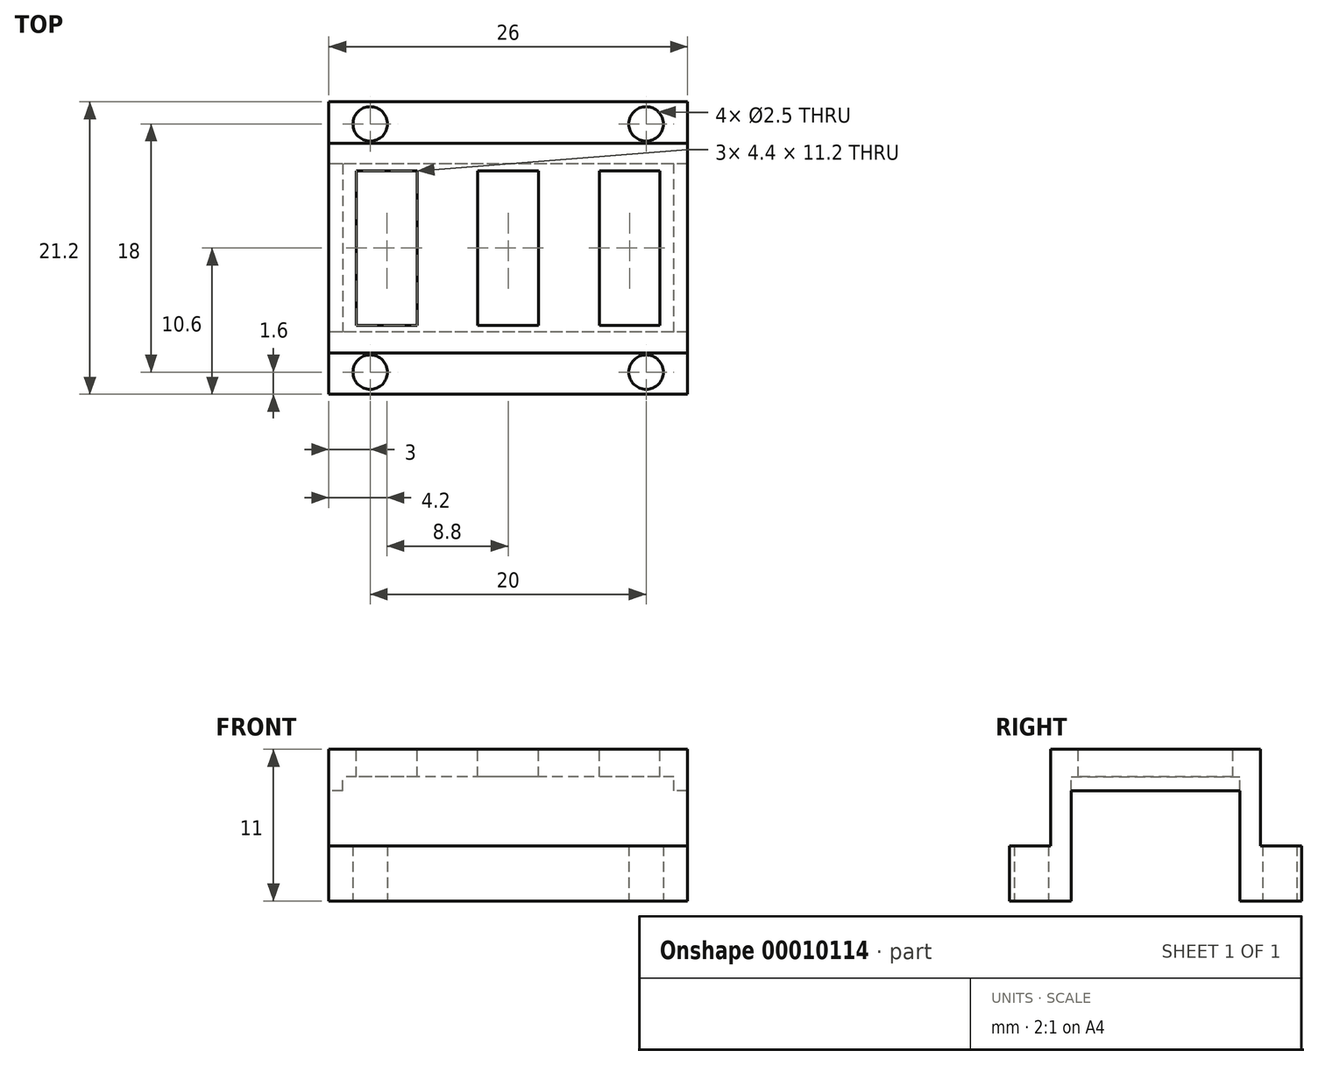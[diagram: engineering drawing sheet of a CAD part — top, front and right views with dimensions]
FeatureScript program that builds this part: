
annotation { "Feature Type Name" : "Feature", "Feature Type Description" : "" }
export const myFeature = defineFeature(function(context is Context, id is Id, definition is map)
    precondition{}
    {
        {
            var Q0;
            Q0=qCreatedBy(makeId("Right.planeOp"),FACE);
            var sketch = newSketch(context, id + "F0", { "sketchPlane" : qUnion([Q0])});
            skLineSegment(sketch, "E0", {"start": v(0, 0) * mm, "end": v(4.5, 0) * mm});
            skLineSegment(sketch, "E1", {"start": v(4.5, 0) * mm, "end": v(4.5, 9) * mm});
            skLineSegment(sketch, "E2", {"start": v(4.5, 9) * mm, "end": v(10.6, 9) * mm});
            skLineSegment(sketch, "E3", {"start": v(10.6, 9) * mm, "end": v(10.6, 11) * mm, "construction": true});
            skLineSegment(sketch, "E4", {"start": v(10.6, 11) * mm, "end": v(3, 11) * mm});
            skLineSegment(sketch, "E5", {"start": v(3, 11) * mm, "end": v(3, 4) * mm});
            skLineSegment(sketch, "E6", {"start": v(3, 4) * mm, "end": v(0, 4) * mm});
            skLineSegment(sketch, "E7", {"start": v(0, 4) * mm, "end": v(0, 0) * mm});
            skLineSegment(sketch, "E8.0.MirrorCS", {"start": v(21.2, 0) * mm, "end": v(16.7, 0) * mm});
            skLineSegment(sketch, "E8.1.MirrorCS", {"start": v(16.7, 0) * mm, "end": v(16.7, 9) * mm});
            skLineSegment(sketch, "E8.2.MirrorCS", {"start": v(16.7, 9) * mm, "end": v(10.6, 9) * mm});
            skLineSegment(sketch, "E8.3.MirrorCS", {"start": v(10.6, 11) * mm, "end": v(18.2, 11) * mm});
            skLineSegment(sketch, "E8.4.MirrorCS", {"start": v(18.2, 11) * mm, "end": v(18.2, 4) * mm});
            skLineSegment(sketch, "E8.5.MirrorCS", {"start": v(21.2, 4) * mm, "end": v(21.2, 0) * mm});
            skLineSegment(sketch, "E8.6.MirrorCS", {"start": v(18.2, 4) * mm, "end": v(21.2, 4) * mm});
            skSolve(sketch);
        }
        {
            var Q0;
            Q0 = qSketchRegion(id + "F0", true);
            extrude(context, id + "F1", {"entities" : qUnion([Q0]), "depth" : 26 * mm});
        }
        {
            var Q0;
            Q0=makeQuery(id+"F1.opExtrude","SWEPT_FACE",FACE,{"disambiguationData":[OSD([sQuery(id+"F0.wireOp",EDGE,"E2"),sQuery(id+"F0.wireOp",EDGE,"E8.2.MirrorCS")])]});
            var sketch = newSketch(context, id + "F2", { "sketchPlane" : qUnion([Q0])});
            skLineSegment(sketch, "E9.bottom", {"start": v(0, -16.7) * mm, "end": v(1, -16.7) * mm});
            skLineSegment(sketch, "E9.top", {"start": v(0, -4.5) * mm, "end": v(1, -4.5) * mm});
            skLineSegment(sketch, "E9.left", {"start": v(0, -16.7) * mm, "end": v(0, -4.5) * mm});
            skLineSegment(sketch, "E9.right", {"start": v(1, -16.7) * mm, "end": v(1, -4.5) * mm});
            skLineSegment(sketch, "E10.bottom", {"start": v(26, -4.5) * mm, "end": v(25, -4.5) * mm});
            skLineSegment(sketch, "E10.top", {"start": v(26, -16.7) * mm, "end": v(25, -16.7) * mm});
            skLineSegment(sketch, "E10.left", {"start": v(26, -4.5) * mm, "end": v(26, -16.7) * mm});
            skLineSegment(sketch, "E10.right", {"start": v(25, -4.5) * mm, "end": v(25, -16.7) * mm});
            skSolve(sketch);
        }
        {
            var Q0;
            Q0 = qSketchRegion(id + "F2", true);
            extrude(context, id + "F3", {"entities" : qUnion([Q0]), "operationType" : NewBodyOperationType.ADD, "depth" : 1 * mm});
        }
        {
            var Q0;
            Q0=makeQuery(id+"F1.opExtrude","SWEPT_FACE",FACE,{"disambiguationData":[OSD([sQuery(id+"F0.wireOp",EDGE,"E0")])]});
            var sketch = newSketch(context, id + "F4", { "sketchPlane" : qUnion([Q0])});
            skCircle(sketch, "E11", {"center": v(3, -1.6) * mm, "radius": 1.25 * mm});
            skLineSegment(sketch, "E12", {"start": v(13, 0) * mm, "end": v(13, -10.6) * mm, "construction": true});
            skLineSegment(sketch, "E13", {"start": v(13, -10.6) * mm, "end": v(0, -10.6) * mm, "construction": true});
            skLineSegment(sketch, "E14", {"start": v(0, -10.6) * mm, "end": v(0, 0) * mm, "construction": true});
            skLineSegment(sketch, "E15", {"start": v(0, -10.6) * mm, "end": v(0, -21.2) * mm, "construction": true});
            skCircle(sketch, "E16.0.MirrorC", {"center": v(23, -1.6) * mm, "radius": 1.25 * mm});
            skCircle(sketch, "E17.0.MirrorC", {"center": v(23, -19.6) * mm, "radius": 1.25 * mm});
            skCircle(sketch, "E17.1.MirrorC", {"center": v(3, -19.6) * mm, "radius": 1.25 * mm});
            skSolve(sketch);
        }
        {
            var Q0;
            Q0 = qSketchRegion(id + "F4", true);
            extrude(context, id + "F5", {"entities" : qUnion([Q0]), "operationType" : NewBodyOperationType.REMOVE, "endBound" : BoundingType.UP_TO_NEXT, "oppositeDirection" : true, "depth" : 25 * mm});
        }
        {
            var Q0;
            Q0=makeQuery(id+"F1.opExtrude","SWEPT_FACE",FACE,{"disambiguationData":[OSD([sQuery(id+"F0.wireOp",EDGE,"E4"),sQuery(id+"F0.wireOp",EDGE,"E8.3.MirrorCS")])]});
            var sketch = newSketch(context, id + "F6", { "sketchPlane" : qUnion([Q0])});
            skLineSegment(sketch, "E18.bottom", {"start": v(6.4, 5) * mm, "end": v(10.8, 5) * mm, "construction": true});
            skLineSegment(sketch, "E18.left", {"start": v(2, 5) * mm, "end": v(2, 16.2) * mm});
            skLineSegment(sketch, "E18.right", {"start": v(10.8, 5) * mm, "end": v(10.8, 16.2) * mm});
            skLineSegment(sketch, "E19.top", {"start": v(10.8, 5) * mm, "end": v(15.2, 5) * mm});
            skLineSegment(sketch, "E19.left", {"start": v(10.8, 16.2) * mm, "end": v(10.8, 5) * mm});
            skLineSegment(sketch, "E20.bottom", {"start": v(15.2, 5) * mm, "end": v(19.6, 5) * mm, "construction": true});
            skLineSegment(sketch, "E20.left", {"start": v(15.2, 5) * mm, "end": v(15.2, 16.2) * mm});
            skLineSegment(sketch, "E20.right", {"start": v(19.6, 5) * mm, "end": v(19.6, 16.2) * mm});
            skLineSegment(sketch, "E21.bottom", {"start": v(19.6, 16.2) * mm, "end": v(24, 16.2) * mm});
            skLineSegment(sketch, "E21.top", {"start": v(19.6, 5) * mm, "end": v(24, 5) * mm});
            skLineSegment(sketch, "E21.left", {"start": v(19.6, 16.2) * mm, "end": v(19.6, 5) * mm});
            skLineSegment(sketch, "E21.right", {"start": v(24, 16.2) * mm, "end": v(24, 5) * mm});
            skLineSegment(sketch, "E22", {"start": v(2, 16.2) * mm, "end": v(0, 16.2) * mm, "construction": true});
            skLineSegment(sketch, "E23", {"start": v(24, 16.2) * mm, "end": v(26, 16.2) * mm, "construction": true});
            skLineSegment(sketch, "E24", {"start": v(13, 16.2) * mm, "end": v(13, 18.2) * mm, "construction": true});
            skLineSegment(sketch, "E25", {"start": v(13, 5) * mm, "end": v(13, 3) * mm, "construction": true});
            skLineSegment(sketch, "E26", {"start": v(6.4, 5) * mm, "end": v(6.4, 16.2) * mm});
            skLineSegment(sketch, "E27", {"start": v(2, 16.2) * mm, "end": v(6.4, 16.2) * mm});
            skLineSegment(sketch, "E28", {"start": v(6.4, 16.2) * mm, "end": v(10.8, 16.2) * mm, "construction": true});
            skLineSegment(sketch, "E29", {"start": v(10.8, 16.2) * mm, "end": v(15.2, 16.2) * mm});
            skLineSegment(sketch, "E30", {"start": v(19.6, 16.2) * mm, "end": v(15.2, 16.2) * mm, "construction": true});
            skLineSegment(sketch, "E31", {"start": v(2, 5) * mm, "end": v(6.4, 5) * mm});
            skSolve(sketch);
        }
        {
            var Q0;
            Q0 = qSketchRegion(id + "F6", true);
            extrude(context, id + "F7", {"entities" : qUnion([Q0]), "operationType" : NewBodyOperationType.REMOVE, "endBound" : BoundingType.UP_TO_NEXT, "oppositeDirection" : true, "depth" : 25 * mm});
        }
    });
